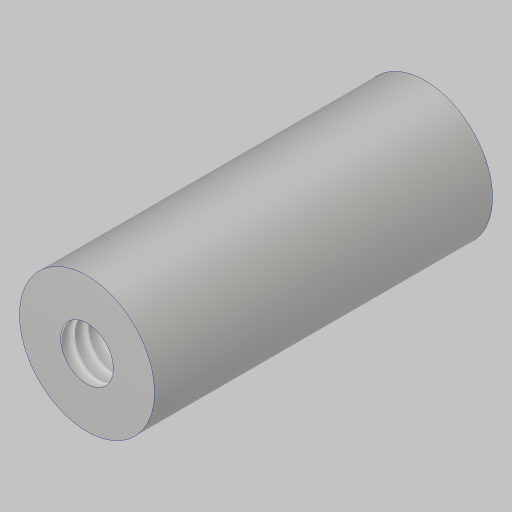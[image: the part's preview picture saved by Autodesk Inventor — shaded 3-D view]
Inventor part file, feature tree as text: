
AUTODESK INVENTOR PART (.ipt)
format: ipt  version: 2023.5 (Build 275446000, 446)  size: 115,712 bytes
history: native  units: in
note: dims shown in document units (in); Inventor stores cm internally (conversion verified against a paired STEP export)
features: sketch x2, extrude x1, hole x1
ambient origin geometry x8: Origin, YZ Plane, XZ Plane, XY Plane, X Axis, Y Axis, Z Axis, Center Point
bodies: Solid1 (feature_tree)
feature tree (4):
  extrude  "Extrusion1"  Depth=1.25in TaperAngle=0.0deg
  hole  "Hole1"  [1 undecoded]
  sketch  "Sketch1"  dims[d0=0.5in d1=1.25in d2=0.0in]
  sketch  "Sketch2"  dims[d3=0.196in d4=0.5in d5=0.507in d6=0.25in d7=0.5635in d8=1.0in d9=0.8108in]
note: 1 required parameter value undecoded (feature->parameter linkage not recoverable at this tier; creation-order binding heuristic only, values carry confidence <= 0.55)
